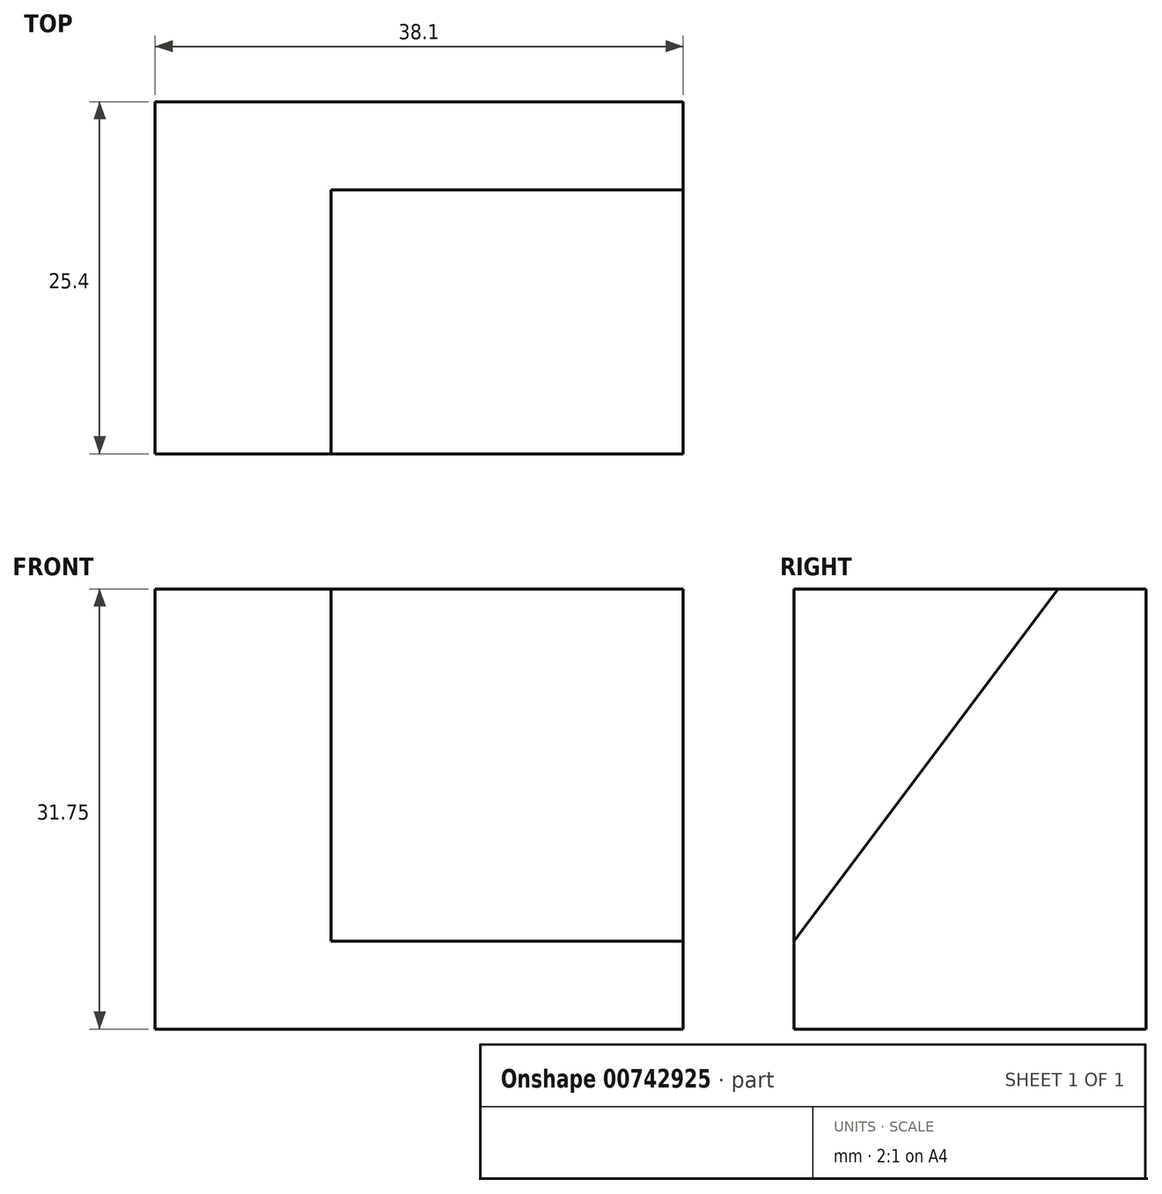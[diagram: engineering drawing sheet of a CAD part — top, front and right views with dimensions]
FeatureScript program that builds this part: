
annotation { "Feature Type Name" : "Feature", "Feature Type Description" : "" }
export const myFeature = defineFeature(function(context is Context, id is Id, definition is map)
    precondition{}
    {
        {
            var Q0;
            Q0=qCreatedBy(makeId("Front.planeOp"),FACE);
            var sketch = newSketch(context, id + "F0", { "sketchPlane" : qUnion([Q0])});
            skLineSegment(sketch, "E0", {"start": v(0, 0) * mm, "end": v(38.1, 0) * mm});
            skLineSegment(sketch, "E1", {"start": v(38.1, 0) * mm, "end": v(38.1, 31.75) * mm});
            skLineSegment(sketch, "E2", {"start": v(38.1, 31.75) * mm, "end": v(0, 31.75) * mm});
            skLineSegment(sketch, "E3", {"start": v(0, 31.75) * mm, "end": v(0, 0) * mm});
            skSolve(sketch);
        }
        {
            var Q0;
            Q0 = qSketchRegion(id + "F0", true);
            extrude(context, id + "F1", {"entities" : qUnion([Q0]), "depth" : 25.4 * mm, "offsetDistance" : 25.4 * mm});
        }
        {
            var Q0;
            Q0=makeQuery(id+"F1.opExtrude","SWEPT_FACE",FACE,{"disambiguationData":[OSD([sQuery(id+"F0.wireOp",EDGE,"E2")])]});
            var sketch = newSketch(context, id + "F2", { "sketchPlane" : qUnion([Q0])});
            skLineSegment(sketch, "E4", {"start": v(12.7, -25.4) * mm, "end": v(12.7, -6.35) * mm});
            skLineSegment(sketch, "E5", {"start": v(12.7, -6.35) * mm, "end": v(38.1, -6.35) * mm});
            skLineSegment(sketch, "E6", {"start": v(38.1, -6.35) * mm, "end": v(38.1, -25.4) * mm});
            skLineSegment(sketch, "E7", {"start": v(38.1, -25.4) * mm, "end": v(12.7, -25.4) * mm});
            skSolve(sketch);
        }
        {
            var Q0;
            Q0 = qSketchRegion(id + "F2", true);
            extrude(context, id + "F3", {"entities" : qUnion([Q0]), "operationType" : NewBodyOperationType.REMOVE, "oppositeDirection" : true, "depth" : 25.4 * mm, "offsetDistance" : 25.4 * mm});
        }
        {
            var Q0;
            Q0=makeQuery(id+"F3.boolean.opBoolean","COPY",FACE,{"derivedFrom":makeQuery(id+"F3.opExtrude","SWEPT_FACE",FACE,{"disambiguationData":[OSD([sQuery(id+"F2.wireOp",EDGE,"E4")])]})});
            var sketch = newSketch(context, id + "F4", { "sketchPlane" : qUnion([Q0])});
            skLineSegment(sketch, "E8", {"start": v(-6.35, 31.75) * mm, "end": v(-25.4, 6.35) * mm});
            skLineSegment(sketch, "E9", {"start": v(-25.4, 6.35) * mm, "end": v(-6.35, 6.35) * mm});
            skLineSegment(sketch, "E10", {"start": v(-6.35, 6.35) * mm, "end": v(-6.35, 31.75) * mm});
            skSolve(sketch);
        }
        {
            var Q0;
            Q0 = qSketchRegion(id + "F4", true);
            extrude(context, id + "F5", {"entities" : qUnion([Q0]), "operationType" : NewBodyOperationType.ADD, "depth" : 25.4 * mm, "offsetDistance" : 25.4 * mm});
        }
    });
